# Revit family: 155561711_Barra Soho
name_source: partatom
category: Furniture
units: mm (PartAtom-declared; Revit-internal decimal feet)

## family parameters
Always vertical = Yes
Cut with Voids When Loaded = No
OmniClass Number = 23.21.23.39
OmniClass Title = Residential Kitchen and Dining Room Furniture
Room Calculation Point = No
Shared = No
Work Plane-Based = No

## types (1)
- Ref. 155561711 BARRA SOHO
    Alto = 993 mm
    Ancho = 1500 mm  [stored 4.92126 ft]
    Carga Máxima = 62 kg.
    Densidad = 15 mms 670 kg./m^3.
    Description = La mejor opción para ampliar la cocina e integrarla al
área socia, práctico mueble que hace juego con la cocina
y alacena SOHO, puede ser utilizada como comedor, además
cuenta con amplios gabinetes y repisas que puedes usar incluso
para elementos de uso cotidiano o decorativos.
Estas dimensiones son nominales y están sujetas a cambios sin previo aviso.
LÍNEA DE ATENCIÓN 01 8000 5120 30
Si usted desea ver nuestra línea completa de productos por favor ingrese a: corona.co
COMPATIBILIDAD CON ELEMENTOS CORONA
SERVICIO
POST VENTA
A SUPERIOR
FRONTAL LATERAL
• Fácil de limpiar
• Resistente al rayado y la abrasión
• Espesores de 15mm en estructura y en puertas dándole mayor
firmeza y robustez.
    Dimensiones generales producto (H * W * D) = 1000 x 1500 x 650 mm.
    Garantía mueble y herrajes = 1 año
    Manufacturer = Corona
    Material A = Corona_Madera_Aglomerada_Miel
    Material B = Corona_Madera_Aglomerada_Plomo
    Peso Neto aprox = 67,2 kg.
    Profundidad = 650 mm  [stored 2.13255 ft]
    Resistencia a la humedad = Hinchamiento < o =8%.
    URL = https://corona.co

note: [stored X ft] marks values corroborated as IEEE doubles in the binary element streams (Revit-internal decimal feet)

## geometry (parser evidence)
native form markers: Sweep x4
no freeform markers — native parametric forms only
